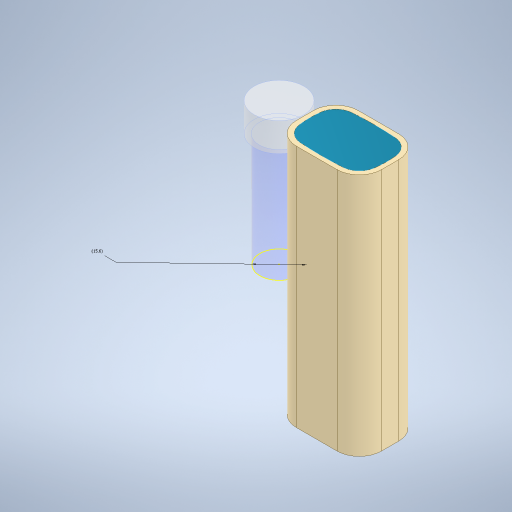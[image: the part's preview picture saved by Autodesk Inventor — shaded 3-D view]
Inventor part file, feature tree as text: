
AUTODESK INVENTOR PART (.ipt)
format: ipt  version: 2023 (Build 270158030, 158C)  size: 374,784 bytes
history: native  units: mm
features: sketch x5, extrude x4, other x3, fillet x1, projected_geometry x1
ambient origin geometry x8: Origin, YZ Plane, XZ Plane, XY Plane, X Axis, Y Axis, Z Axis, Center Point
bodies: Body1 (feature_tree), Body2 (feature_tree), Body3 (feature_tree)
feature tree (14):
  other  "vape"
  extrude  "Extrusion1"  Depth=15.5mm
  fillet  "Fillet1"  Radius=21.6mm
  extrude  "Extrusion2"  Depth=98.5mm TaperAngle=0.0deg
  extrude  "Extrusion3"  Depth=15.5mm
  extrude  "Extrusion4"  Depth=7.0mm
  sketch  "Sketch5"  dims[d10=2.0mm d13=1.55mm d14=1.4mm d15=3.0mm d17=2.0mm d18=2.0mm d19=2.0mm d20=2.0mm d21=9.0mm d22=5.0mm d23=0.0mm d24=20.0mm d25=10.5mm d26=11.6mm d27=0.0mm d28=15.92mm d29=45.8mm d30=-0.034907mm d31=15.600254mm]
  sketch  "Sketch1"  dims[d0=31.0mm d1=15.5mm d2=21.6mm]
  sketch  "Sketch2"  dims[d3=10.8mm d4=98.5mm d5=0.0mm]
  projected_geometry  "Projected Loop1"
  other  "vape-tube"
  sketch  "Sketch3"  dims[d6=1.0mm d7=15.5mm]
  other  "storage"
  sketch  "Sketch4"  dims[d8=2.0mm d9=7.0mm]
